# Revit family: Haworth_Masters_Desk_KeystoneHalf
name_source: partatom
category: Furniture Systems
revit_build: Autodesk Revit 2018 (Build: 20170223_1515(x64)
units: mm (PartAtom-declared; Revit-internal decimal feet)

## family parameters
Always vertical = Yes
Cut with Voids When Loaded = No
OmniClass Number = 23.40.70.14.64.21
OmniClass Title = Systems Furniture
Part Type = Normal
Room Calculation Point = No
Round Connector Dimension = Use Diameter
Shared = No
Work Plane-Based = No

## types (3) — shared parameters
Actual Height = 29 1/8"
Assembly Code = E2020200
Column Support = Yes
Custom Size = No
Depth Small Offset = 12"
Description = Haworth - Masters Desk - Keystone - Half
Edge Finish = Haworth _ Wood _ White Oak
Manufacturer = Haworth
Max. Depth = 48"
Max. Width = 72"
Min. Depth = 42"
Min. Width = 60"
Model = Haworth - Masters Desk - Keystone - Half
Post Finish = Haworth _ Paint _ Metallic Champagne
Post Position = 18"
Revision Number = 2
Size = Verify Final Dim. w/ Haworth
Stanchions = Yes
Standard Sizes = 42x60, 45x66, 48x72 in.
Support Height = 22 3/4"
Support Position = 13"
Support Position Right = 19"
Sustainability Info = http://www.haworth.com
URL = www.haworth.com
URL - Product = http://www.haworth.com
Warranty = http://www.haworth.com
Worksurface Finish = Haworth _ Wood _ White Oak

## per-type parameters (varying)
| type | Actual Depth Large | Actual Width | Depth Large | Width |
| 48d 72w | 48" | 72" | 48" | 72" |
| 45d 66w | 45" | 66" | 45" | 66" |
| 42d 60w | 42" | 60" | 42" | 60" |

## geometry (parser evidence)
native form markers: Sweep x6
no freeform markers — native parametric forms only
